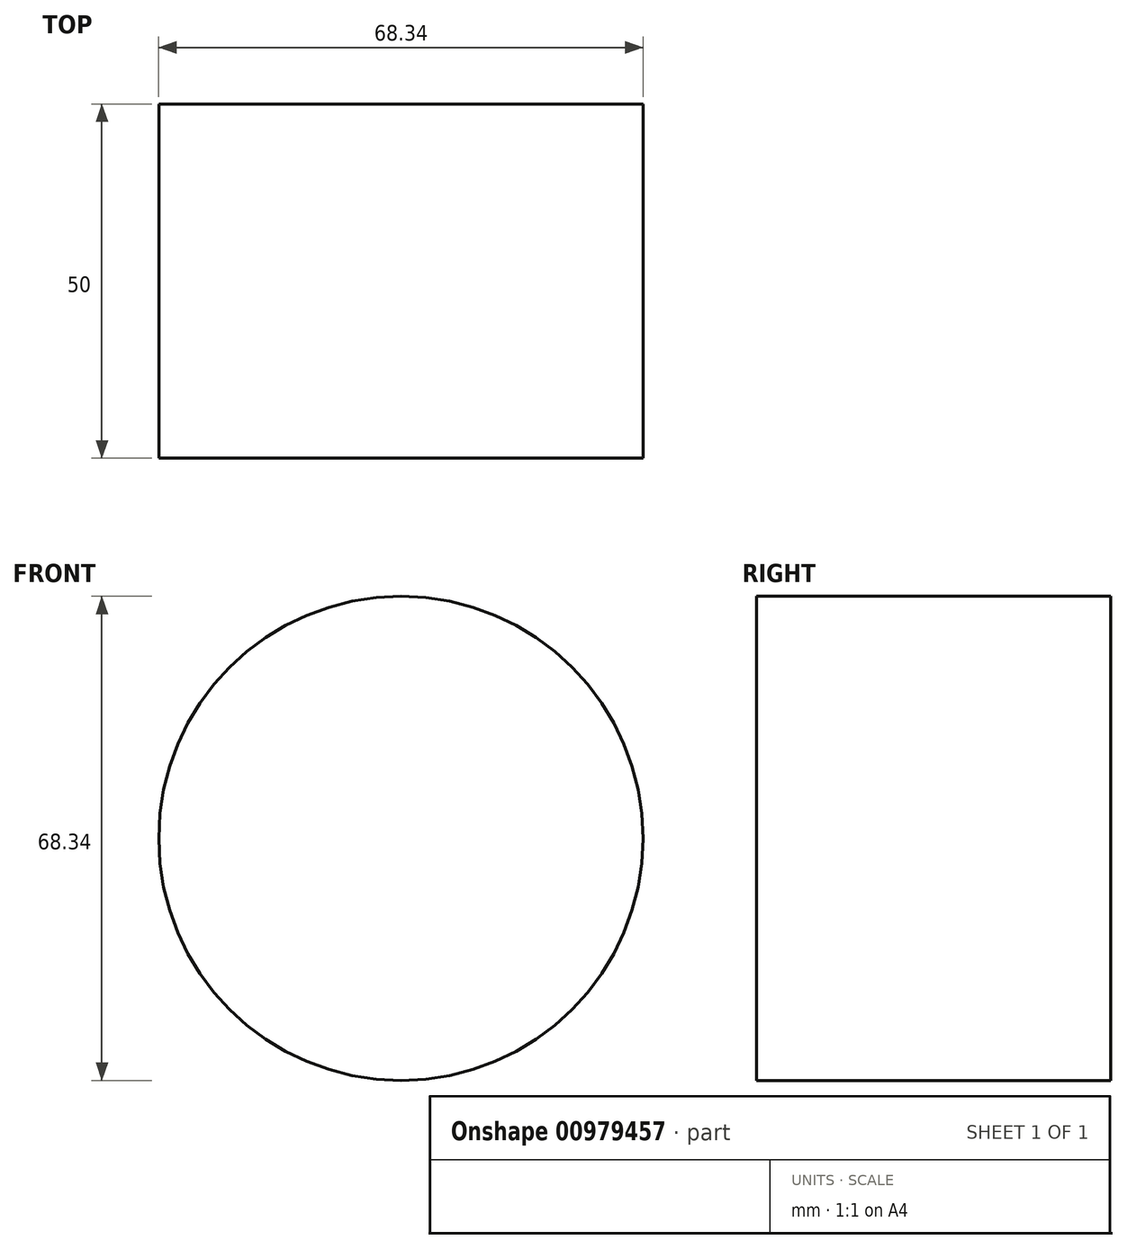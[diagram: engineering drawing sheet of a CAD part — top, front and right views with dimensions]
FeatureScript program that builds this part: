
annotation { "Feature Type Name" : "Feature", "Feature Type Description" : "" }
export const myFeature = defineFeature(function(context is Context, id is Id, definition is map)
    precondition{}
    {
        {
            var Q0;
            Q0=qCreatedBy(makeId("Front.planeOp"),FACE);
            var sketch = newSketch(context, id + "F0", { "sketchPlane" : qUnion([Q0])});
            skCircle(sketch, "E0", {"center": v(0, 0) * mm, "radius": 34.17 * mm});
            skSolve(sketch);
        }
        {
            var Q0;
            Q0=makeQuery(id+"F0.imprint","IMPRINT",FACE,{"disambiguationData":[TD([[makeQuery(id+"F0.imprint","IMPRINT",EDGE,{"derivedFrom":sQuery(id+"F0.wireOp",EDGE,"E0")}),1.0]])]});
            extrude(context, id + "F1", {"entities" : qUnion([Q0]), "depth" : 25 * mm, "offsetDistance" : 25 * mm, "hasSecondDirection" : true, "secondDirectionOppositeDirection" : true, "secondDirectionDepth" : 25 * mm});
        }
    });
